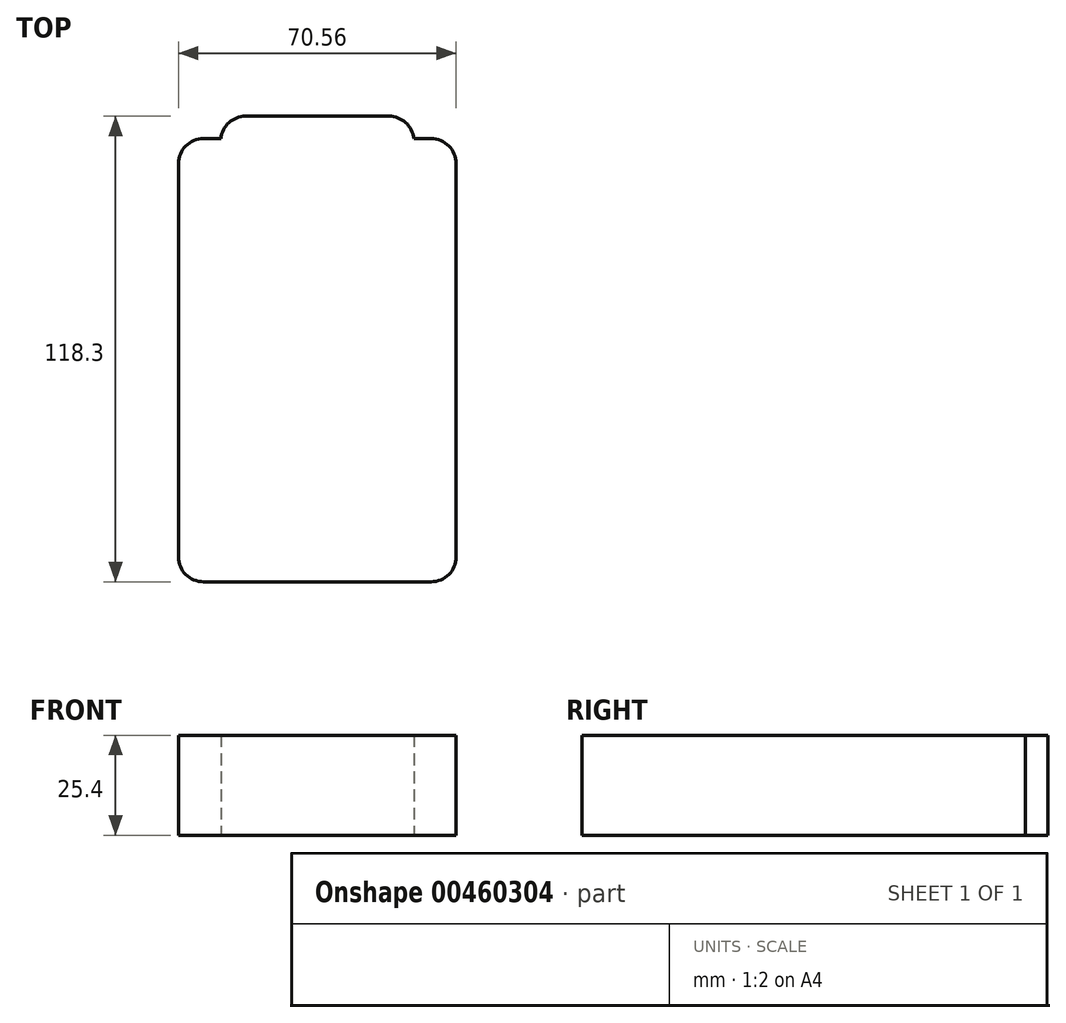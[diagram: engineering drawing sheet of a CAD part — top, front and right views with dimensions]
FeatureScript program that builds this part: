
annotation { "Feature Type Name" : "Feature", "Feature Type Description" : "" }
export const myFeature = defineFeature(function(context is Context, id is Id, definition is map)
    precondition{}
    {
        {
            var Q0;
            Q0=qCreatedBy(makeId("Top.planeOp"),FACE);
            var sketch = newSketch(context, id + "F0", { "sketchPlane" : qUnion([Q0])});
            skLineSegment(sketch, "E0.bottom", {"start": v(28.93, 56.3) * mm, "end": v(-28.93, 56.3) * mm});
            skLineSegment(sketch, "E0.top", {"start": v(28.93, -56.3) * mm, "end": v(-28.93, -56.3) * mm});
            skLineSegment(sketch, "E0.left", {"start": v(35.28, 49.94) * mm, "end": v(35.28, -49.94) * mm});
            skLineSegment(sketch, "E0.right", {"start": v(-35.28, 49.94) * mm, "end": v(-35.28, -49.94) * mm});
            skPoint(sketch, "E0.middle", {"position": v(0, 0) * mm});
            skPoint(sketch, "E1.visualSharp", {"position": v(-35.28, 56.3) * mm});
            skArc(sketch, "E1.filletArc", {"start": v(-28.93, 56.3) * mm, "mid": v(-33.42, 54.43) * mm, "end": v(-35.28, 49.94) * mm});
            skPoint(sketch, "E2.visualSharp", {"position": v(35.28, 56.3) * mm});
            skArc(sketch, "E2.filletArc", {"start": v(35.28, 49.94) * mm, "mid": v(33.42, 54.43) * mm, "end": v(28.93, 56.3) * mm});
            skPoint(sketch, "E3.visualSharp", {"position": v(35.28, -56.3) * mm});
            skArc(sketch, "E3.filletArc", {"start": v(28.93, -56.3) * mm, "mid": v(33.42, -54.43) * mm, "end": v(35.28, -49.94) * mm});
            skPoint(sketch, "E4.visualSharp", {"position": v(-35.28, -56.3) * mm});
            skArc(sketch, "E4.filletArc", {"start": v(-35.28, -49.94) * mm, "mid": v(-33.42, -54.43) * mm, "end": v(-28.93, -56.3) * mm});
            skLineSegment(sketch, "E5.bottom", {"start": v(-18.2, 62.01) * mm, "end": v(18.2, 62.01) * mm});
            skLineSegment(sketch, "E5.top", {"start": v(-24.54, 50.57) * mm, "end": v(24.54, 50.57) * mm});
            skLineSegment(sketch, "E5.left", {"start": v(-24.54, 55.66) * mm, "end": v(-24.54, 50.57) * mm});
            skLineSegment(sketch, "E5.right", {"start": v(24.54, 55.66) * mm, "end": v(24.54, 50.57) * mm});
            skPoint(sketch, "E5.middle", {"position": v(0, 56.3) * mm});
            skPoint(sketch, "E6.visualSharp", {"position": v(-24.54, 62.01) * mm});
            skArc(sketch, "E6.filletArc", {"start": v(-18.2, 62.01) * mm, "mid": v(-22.68, 60.15) * mm, "end": v(-24.54, 55.66) * mm});
            skPoint(sketch, "E7.visualSharp", {"position": v(24.54, 62.01) * mm});
            skArc(sketch, "E7.filletArc", {"start": v(24.54, 55.66) * mm, "mid": v(22.68, 60.15) * mm, "end": v(18.2, 62.01) * mm});
            skSolve(sketch);
        }
        {
            var Q0;
            Q0=makeQuery(id+"F0.imprint","IMPRINT",FACE,{"disambiguationData":[TD([[makeQuery(id+"F0.imprint","IMPRINT",EDGE,{"derivedFrom":sQuery(id+"F0.wireOp",EDGE,"E5.top")}),1.0]])]});
            var Q1;
            Q1=makeQuery(id+"F0.imprint","IMPRINT",FACE,{"disambiguationData":[TD([[makeQuery(id+"F0.imprint","IMPRINT",EDGE,{"derivedFrom":sQuery(id+"F0.wireOp",EDGE,"E0.top")}),-1.0]])]});
            var Q2;
            {var subQ5=sQuery(id+"F0.wireOp",EDGE,"E5.bottom");Q2=makeQuery(id+"F0.imprint","IMPRINT",FACE,{"disambiguationData":[TD([[makeQuery(id+"F0.imprint","IMPRINT",EDGE,{"derivedFrom":subQ5}),-1.0]])]});}
            extrude(context, id + "F1", {"entities" : qUnion([Q0, Q1, Q2]), "depth" : 25.4 * mm});
        }
    });
